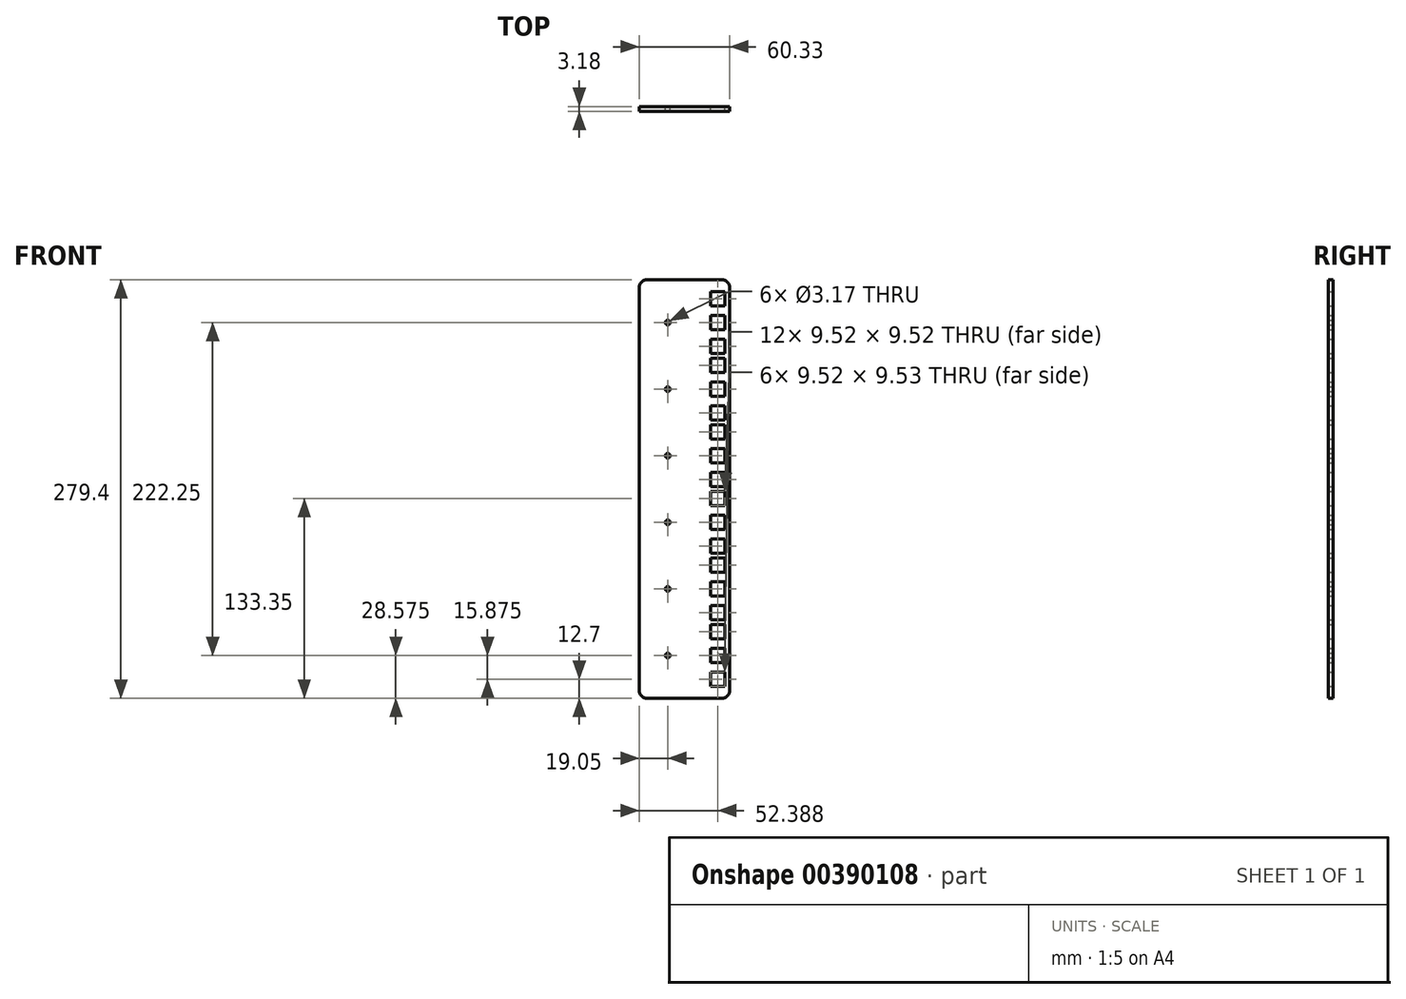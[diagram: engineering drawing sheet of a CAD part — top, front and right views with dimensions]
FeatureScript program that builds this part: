
annotation { "Feature Type Name" : "Feature", "Feature Type Description" : "" }
export const myFeature = defineFeature(function(context is Context, id is Id, definition is map)
    precondition{}
    {
        {
            var Q0;
            Q0=qCreatedBy(makeId("Front.planeOp"),FACE);
            var sketch = newSketch(context, id + "F0", { "sketchPlane" : qUnion([Q0])});
            skLineSegment(sketch, "E0.bottom", {"start": v(0, 0) * mm, "end": v(60.33, 0) * mm});
            skLineSegment(sketch, "E0.top", {"start": v(0, 279.4) * mm, "end": v(60.32, 279.4) * mm});
            skLineSegment(sketch, "E0.left", {"start": v(0, 0) * mm, "end": v(0, 279.4) * mm});
            skLineSegment(sketch, "E0.right", {"start": v(60.33, 0) * mm, "end": v(60.33, 279.4) * mm});
            skLineSegment(sketch, "E1", {"start": v(44.45, 279.4) * mm, "end": v(44.45, 0) * mm, "construction": true});
            skLineSegment(sketch, "E2", {"start": v(52.39, 279.4) * mm, "end": v(52.39, 0) * mm, "construction": true});
            skLineSegment(sketch, "E3.bottom", {"start": v(57.15, 271.46) * mm, "end": v(47.62, 271.46) * mm});
            skLineSegment(sketch, "E3.top", {"start": v(57.15, 261.94) * mm, "end": v(47.62, 261.94) * mm});
            skLineSegment(sketch, "E3.left", {"start": v(57.15, 271.46) * mm, "end": v(57.15, 261.94) * mm});
            skLineSegment(sketch, "E3.right", {"start": v(47.62, 271.46) * mm, "end": v(47.62, 261.94) * mm});
            skPoint(sketch, "E3.middle", {"position": v(52.39, 266.7) * mm});
            skLineSegment(sketch, "E4.0.1.0", {"start": v(57.15, 255.59) * mm, "end": v(47.62, 255.59) * mm});
            skLineSegment(sketch, "E4.0.1.1", {"start": v(57.15, 255.59) * mm, "end": v(57.15, 246.06) * mm});
            skLineSegment(sketch, "E4.0.1.2", {"start": v(47.62, 255.59) * mm, "end": v(47.62, 246.06) * mm});
            skLineSegment(sketch, "E4.0.1.3", {"start": v(57.15, 246.06) * mm, "end": v(47.62, 246.06) * mm});
            skLineSegment(sketch, "E4.0.2.0", {"start": v(57.15, 239.71) * mm, "end": v(47.62, 239.71) * mm});
            skLineSegment(sketch, "E4.0.2.1", {"start": v(57.15, 239.71) * mm, "end": v(57.15, 230.19) * mm});
            skLineSegment(sketch, "E4.0.2.2", {"start": v(47.62, 239.71) * mm, "end": v(47.62, 230.19) * mm});
            skLineSegment(sketch, "E4.0.2.3", {"start": v(57.15, 230.19) * mm, "end": v(47.62, 230.19) * mm});
            skLineSegment(sketch, "E4.direction1", {"start": v(47.62, 261.94) * mm, "end": v(73.02, 261.94) * mm, "construction": true});
            skLineSegment(sketch, "E4.direction2", {"start": v(47.62, 261.94) * mm, "end": v(47.62, 246.06) * mm, "construction": true});
            skLineSegment(sketch, "E5.0.1.0", {"start": v(47.62, 217.49) * mm, "end": v(47.62, 201.61) * mm, "construction": true});
            skLineSegment(sketch, "E5.0.1.1", {"start": v(57.15, 185.74) * mm, "end": v(47.62, 185.74) * mm});
            skLineSegment(sketch, "E5.0.1.2", {"start": v(57.15, 201.61) * mm, "end": v(47.62, 201.61) * mm});
            skPoint(sketch, "E5.0.1.3", {"position": v(52.39, 222.25) * mm});
            skLineSegment(sketch, "E5.0.1.4", {"start": v(57.15, 195.26) * mm, "end": v(47.62, 195.26) * mm});
            skLineSegment(sketch, "E5.0.1.5", {"start": v(57.15, 195.26) * mm, "end": v(57.15, 185.74) * mm});
            skLineSegment(sketch, "E5.0.1.6", {"start": v(57.15, 227.01) * mm, "end": v(47.62, 227.01) * mm});
            skLineSegment(sketch, "E5.0.1.7", {"start": v(57.15, 227.01) * mm, "end": v(57.15, 217.49) * mm});
            skLineSegment(sketch, "E5.0.1.8", {"start": v(47.62, 227.01) * mm, "end": v(47.62, 217.49) * mm});
            skLineSegment(sketch, "E5.0.1.9", {"start": v(57.15, 211.14) * mm, "end": v(47.62, 211.14) * mm});
            skLineSegment(sketch, "E5.0.1.10", {"start": v(57.15, 211.14) * mm, "end": v(57.15, 201.61) * mm});
            skLineSegment(sketch, "E5.0.1.11", {"start": v(47.62, 217.49) * mm, "end": v(73.02, 217.49) * mm, "construction": true});
            skLineSegment(sketch, "E5.0.1.12", {"start": v(47.62, 195.26) * mm, "end": v(47.62, 185.74) * mm});
            skLineSegment(sketch, "E5.0.1.13", {"start": v(57.15, 217.49) * mm, "end": v(47.62, 217.49) * mm});
            skLineSegment(sketch, "E5.0.1.14", {"start": v(47.62, 211.14) * mm, "end": v(47.62, 201.61) * mm});
            skLineSegment(sketch, "E5.0.2.0", {"start": v(47.62, 173.04) * mm, "end": v(47.62, 157.16) * mm, "construction": true});
            skLineSegment(sketch, "E5.0.2.1", {"start": v(57.15, 141.29) * mm, "end": v(47.62, 141.29) * mm});
            skLineSegment(sketch, "E5.0.2.2", {"start": v(57.15, 157.16) * mm, "end": v(47.62, 157.16) * mm});
            skPoint(sketch, "E5.0.2.3", {"position": v(52.39, 177.8) * mm});
            skLineSegment(sketch, "E5.0.2.4", {"start": v(57.15, 150.81) * mm, "end": v(47.62, 150.81) * mm});
            skLineSegment(sketch, "E5.0.2.5", {"start": v(57.15, 150.81) * mm, "end": v(57.15, 141.29) * mm});
            skLineSegment(sketch, "E5.0.2.6", {"start": v(57.15, 182.56) * mm, "end": v(47.62, 182.56) * mm});
            skLineSegment(sketch, "E5.0.2.7", {"start": v(57.15, 182.56) * mm, "end": v(57.15, 173.04) * mm});
            skLineSegment(sketch, "E5.0.2.8", {"start": v(47.62, 182.56) * mm, "end": v(47.62, 173.04) * mm});
            skLineSegment(sketch, "E5.0.2.9", {"start": v(57.15, 166.69) * mm, "end": v(47.62, 166.69) * mm});
            skLineSegment(sketch, "E5.0.2.10", {"start": v(57.15, 166.69) * mm, "end": v(57.15, 157.16) * mm});
            skLineSegment(sketch, "E5.0.2.11", {"start": v(47.62, 173.04) * mm, "end": v(73.02, 173.04) * mm, "construction": true});
            skLineSegment(sketch, "E5.0.2.12", {"start": v(47.62, 150.81) * mm, "end": v(47.62, 141.29) * mm});
            skLineSegment(sketch, "E5.0.2.13", {"start": v(57.15, 173.04) * mm, "end": v(47.62, 173.04) * mm});
            skLineSegment(sketch, "E5.0.2.14", {"start": v(47.62, 166.69) * mm, "end": v(47.62, 157.16) * mm});
            skLineSegment(sketch, "E5.0.3.0", {"start": v(47.62, 128.59) * mm, "end": v(47.62, 112.71) * mm, "construction": true});
            skLineSegment(sketch, "E5.0.3.1", {"start": v(57.15, 96.84) * mm, "end": v(47.62, 96.84) * mm});
            skLineSegment(sketch, "E5.0.3.2", {"start": v(57.15, 112.71) * mm, "end": v(47.62, 112.71) * mm});
            skPoint(sketch, "E5.0.3.3", {"position": v(52.39, 133.35) * mm});
            skLineSegment(sketch, "E5.0.3.4", {"start": v(57.15, 106.36) * mm, "end": v(47.62, 106.36) * mm});
            skLineSegment(sketch, "E5.0.3.5", {"start": v(57.15, 106.36) * mm, "end": v(57.15, 96.84) * mm});
            skLineSegment(sketch, "E5.0.3.6", {"start": v(57.15, 138.11) * mm, "end": v(47.62, 138.11) * mm});
            skLineSegment(sketch, "E5.0.3.7", {"start": v(57.15, 138.11) * mm, "end": v(57.15, 128.59) * mm});
            skLineSegment(sketch, "E5.0.3.8", {"start": v(47.62, 138.11) * mm, "end": v(47.62, 128.59) * mm});
            skLineSegment(sketch, "E5.0.3.9", {"start": v(57.15, 122.24) * mm, "end": v(47.62, 122.24) * mm});
            skLineSegment(sketch, "E5.0.3.10", {"start": v(57.15, 122.24) * mm, "end": v(57.15, 112.71) * mm});
            skLineSegment(sketch, "E5.0.3.11", {"start": v(47.62, 128.59) * mm, "end": v(73.02, 128.59) * mm, "construction": true});
            skLineSegment(sketch, "E5.0.3.12", {"start": v(47.62, 106.36) * mm, "end": v(47.62, 96.84) * mm});
            skLineSegment(sketch, "E5.0.3.13", {"start": v(57.15, 128.59) * mm, "end": v(47.62, 128.59) * mm});
            skLineSegment(sketch, "E5.0.3.14", {"start": v(47.62, 122.24) * mm, "end": v(47.62, 112.71) * mm});
            skLineSegment(sketch, "E5.0.4.0", {"start": v(47.62, 84.14) * mm, "end": v(47.62, 68.26) * mm, "construction": true});
            skLineSegment(sketch, "E5.0.4.1", {"start": v(57.15, 52.39) * mm, "end": v(47.62, 52.39) * mm});
            skLineSegment(sketch, "E5.0.4.2", {"start": v(57.15, 68.26) * mm, "end": v(47.62, 68.26) * mm});
            skPoint(sketch, "E5.0.4.3", {"position": v(52.39, 88.9) * mm});
            skLineSegment(sketch, "E5.0.4.4", {"start": v(57.15, 61.91) * mm, "end": v(47.62, 61.91) * mm});
            skLineSegment(sketch, "E5.0.4.5", {"start": v(57.15, 61.91) * mm, "end": v(57.15, 52.39) * mm});
            skLineSegment(sketch, "E5.0.4.6", {"start": v(57.15, 93.66) * mm, "end": v(47.62, 93.66) * mm});
            skLineSegment(sketch, "E5.0.4.7", {"start": v(57.15, 93.66) * mm, "end": v(57.15, 84.14) * mm});
            skLineSegment(sketch, "E5.0.4.8", {"start": v(47.62, 93.66) * mm, "end": v(47.62, 84.14) * mm});
            skLineSegment(sketch, "E5.0.4.9", {"start": v(57.15, 77.79) * mm, "end": v(47.62, 77.79) * mm});
            skLineSegment(sketch, "E5.0.4.10", {"start": v(57.15, 77.79) * mm, "end": v(57.15, 68.26) * mm});
            skLineSegment(sketch, "E5.0.4.11", {"start": v(47.62, 84.14) * mm, "end": v(73.02, 84.14) * mm, "construction": true});
            skLineSegment(sketch, "E5.0.4.12", {"start": v(47.62, 61.91) * mm, "end": v(47.62, 52.39) * mm});
            skLineSegment(sketch, "E5.0.4.13", {"start": v(57.15, 84.14) * mm, "end": v(47.62, 84.14) * mm});
            skLineSegment(sketch, "E5.0.4.14", {"start": v(47.62, 77.79) * mm, "end": v(47.62, 68.26) * mm});
            skLineSegment(sketch, "E5.0.5.0", {"start": v(47.62, 39.69) * mm, "end": v(47.62, 23.81) * mm, "construction": true});
            skLineSegment(sketch, "E5.0.5.1", {"start": v(57.15, 7.94) * mm, "end": v(47.62, 7.94) * mm});
            skLineSegment(sketch, "E5.0.5.2", {"start": v(57.15, 23.81) * mm, "end": v(47.62, 23.81) * mm});
            skPoint(sketch, "E5.0.5.3", {"position": v(52.39, 44.45) * mm});
            skLineSegment(sketch, "E5.0.5.4", {"start": v(57.15, 17.46) * mm, "end": v(47.62, 17.46) * mm});
            skLineSegment(sketch, "E5.0.5.5", {"start": v(57.15, 17.46) * mm, "end": v(57.15, 7.94) * mm});
            skLineSegment(sketch, "E5.0.5.6", {"start": v(57.15, 49.21) * mm, "end": v(47.62, 49.21) * mm});
            skLineSegment(sketch, "E5.0.5.7", {"start": v(57.15, 49.21) * mm, "end": v(57.15, 39.69) * mm});
            skLineSegment(sketch, "E5.0.5.8", {"start": v(47.62, 49.21) * mm, "end": v(47.62, 39.69) * mm});
            skLineSegment(sketch, "E5.0.5.9", {"start": v(57.15, 33.34) * mm, "end": v(47.62, 33.34) * mm});
            skLineSegment(sketch, "E5.0.5.10", {"start": v(57.15, 33.34) * mm, "end": v(57.15, 23.81) * mm});
            skLineSegment(sketch, "E5.0.5.11", {"start": v(47.62, 39.69) * mm, "end": v(73.02, 39.69) * mm, "construction": true});
            skLineSegment(sketch, "E5.0.5.12", {"start": v(47.62, 17.46) * mm, "end": v(47.62, 7.94) * mm});
            skLineSegment(sketch, "E5.0.5.13", {"start": v(57.15, 39.69) * mm, "end": v(47.62, 39.69) * mm});
            skLineSegment(sketch, "E5.0.5.14", {"start": v(47.62, 33.34) * mm, "end": v(47.62, 23.81) * mm});
            skLineSegment(sketch, "E5.direction1", {"start": v(47.62, 230.19) * mm, "end": v(73.02, 230.19) * mm, "construction": true});
            skLineSegment(sketch, "E5.direction2", {"start": v(47.62, 230.19) * mm, "end": v(47.62, 185.74) * mm, "construction": true});
            skLineSegment(sketch, "E6", {"start": v(47.62, 230.19) * mm, "end": v(57.15, 239.71) * mm, "construction": true});
            skLineSegment(sketch, "E7", {"start": v(52.39, 234.95) * mm, "end": v(57.15, 230.19) * mm, "construction": true});
            skLineSegment(sketch, "E8", {"start": v(57.15, 17.46) * mm, "end": v(52.39, 12.7) * mm, "construction": true});
            skPoint(sketch, "E8.endSnap0", {"position": v(57.15, 12.7) * mm});
            skLineSegment(sketch, "E9", {"start": v(19.05, 279.4) * mm, "end": v(19.05, 0) * mm, "construction": true});
            skCircle(sketch, "E10", {"center": v(19.05, 250.83) * mm, "radius": 1.59 * mm});
            skLineSegment(sketch, "E11", {"start": v(0, 139.7) * mm, "end": v(19.05, 139.7) * mm, "construction": true});
            skLineSegment(sketch, "E12", {"start": v(19.05, 250.83) * mm, "end": v(47.62, 250.83) * mm, "construction": true});
            skCircle(sketch, "E13.0.1.0", {"center": v(19.05, 206.38) * mm, "radius": 1.59 * mm});
            skCircle(sketch, "E13.0.2.0", {"center": v(19.05, 161.93) * mm, "radius": 1.59 * mm});
            skCircle(sketch, "E13.0.3.0", {"center": v(19.05, 117.48) * mm, "radius": 1.59 * mm});
            skCircle(sketch, "E13.0.4.0", {"center": v(19.05, 73.03) * mm, "radius": 1.59 * mm});
            skCircle(sketch, "E13.0.5.0", {"center": v(19.05, 28.58) * mm, "radius": 1.59 * mm});
            skLineSegment(sketch, "E13.direction1", {"start": v(19.05, 250.83) * mm, "end": v(44.45, 250.83) * mm, "construction": true});
            skLineSegment(sketch, "E13.direction2", {"start": v(19.05, 250.83) * mm, "end": v(19.05, 206.38) * mm, "construction": true});
            skSolve(sketch);
        }
        {
            var Q0;
            Q0=makeQuery(id+"F0.imprint","IMPRINT",FACE,{"disambiguationData":[TD([[makeQuery(id+"F0.imprint","IMPRINT",EDGE,{"derivedFrom":sQuery(id+"F0.wireOp",EDGE,"E0.bottom")}),1.0]])]});
            extrude(context, id + "F1", {"entities" : qUnion([Q0]), "depth" : 3.17 * mm});
        }
        {
            var Q0;
            Q0=makeQuery(id+"F1.opExtrude","SWEPT_EDGE",EDGE,{"disambiguationData":[OSD([sQuery(id+"F0.wireOp",EDGE,"E0.top"),sQuery(id+"F0.wireOp",EDGE,"E0.left")])]});
            var Q1;
            Q1=makeQuery(id+"F1.opExtrude","SWEPT_EDGE",EDGE,{"disambiguationData":[OSD([sQuery(id+"F0.wireOp",EDGE,"E0.top"),sQuery(id+"F0.wireOp",EDGE,"E0.right")])]});
            var Q2;
            Q2=makeQuery(id+"F1.opExtrude","SWEPT_EDGE",EDGE,{"disambiguationData":[OSD([sQuery(id+"F0.wireOp",EDGE,"E0.bottom"),sQuery(id+"F0.wireOp",EDGE,"E0.left")])]});
            var Q3;
            Q3=makeQuery(id+"F1.opExtrude","SWEPT_EDGE",EDGE,{"disambiguationData":[OSD([sQuery(id+"F0.wireOp",EDGE,"E0.bottom"),sQuery(id+"F0.wireOp",EDGE,"E0.right")])]});
            fillet(context, id + "F2", {"entities" : qUnion([Q0, Q1, Q2, Q3]), "radius" : 5.08 * mm, "tangentPropagation" : true, "allowEdgeOverflow" : false});
        }
    });
